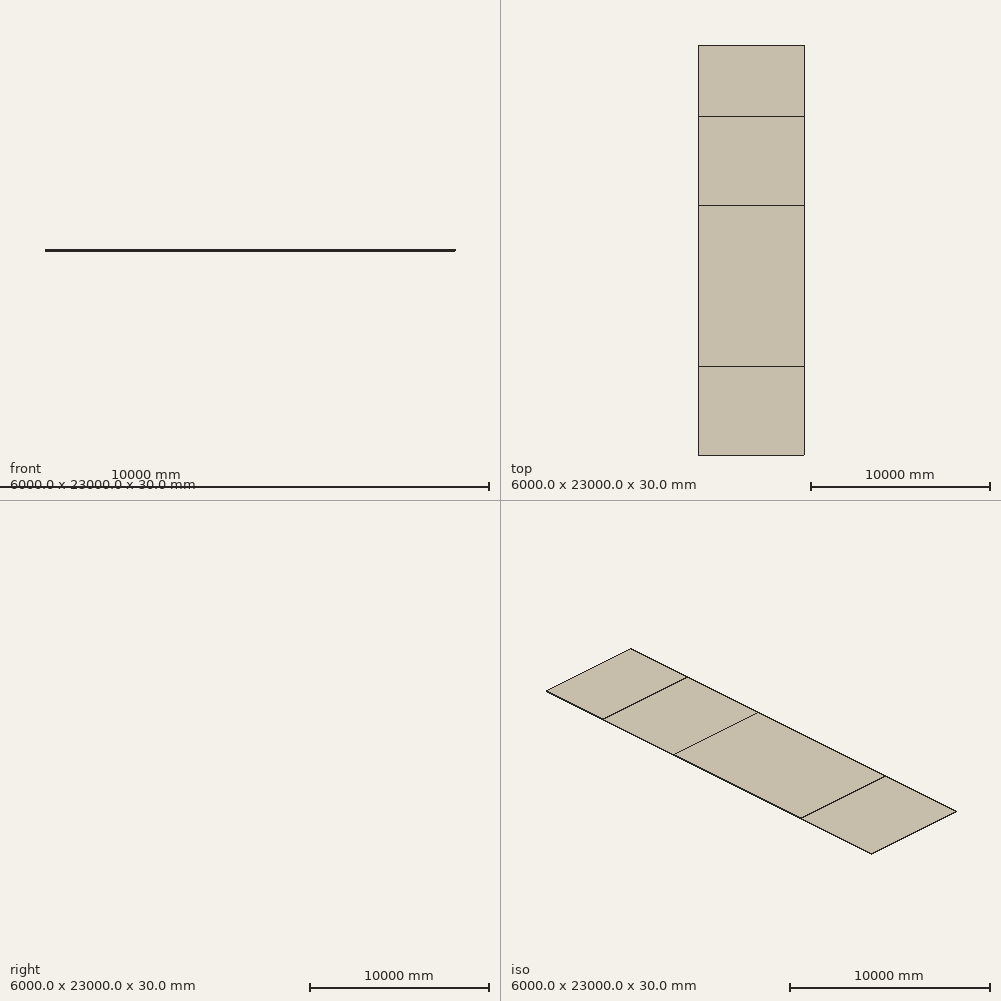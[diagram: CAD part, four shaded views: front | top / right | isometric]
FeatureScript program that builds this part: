
annotation { "Feature Type Name" : "Feature", "Feature Type Description" : "" }
export const myFeature = defineFeature(function(context is Context, id is Id, definition is map)
    precondition{}
    {
        {
            var Q0;
            Q0=qCreatedBy(makeId("Top.planeOp"),FACE);
            var sketch = newSketch(context, id + "F0", { "sketchPlane" : qUnion([Q0])});
            skLineSegment(sketch, "E0.bottom", {"start": v(0, 0) * mm, "end": v(-6000, 0) * mm});
            skLineSegment(sketch, "E0.top", {"start": v(0, 23000) * mm, "end": v(-6000, 23000) * mm});
            skLineSegment(sketch, "E0.left", {"start": v(0, 0) * mm, "end": v(0, 23000) * mm});
            skLineSegment(sketch, "E0.right", {"start": v(-6000, 0) * mm, "end": v(-6000, 23000) * mm});
            skSolve(sketch);
        }
        {
            var Q0;
            Q0=makeQuery(id+"F0.imprint","IMPRINT",FACE,{"disambiguationData":[TD([[makeQuery(id+"F0.imprint","IMPRINT",EDGE,{"derivedFrom":sQuery(id+"F0.wireOp",EDGE,"E0.bottom")}),-1.0]])]});
            extrude(context, id + "F1", {"entities" : qUnion([Q0]), "depth" : 30 * mm, "offsetDistance" : 25 * mm});
        }
        {
            var Q0;
            Q0=makeQuery(id+"F1.opExtrude","CAP_FACE",FACE,{"disambiguationData":[OSD([sQuery(id+"F0.wireOp",EDGE,"E0.bottom"),sQuery(id+"F0.wireOp",EDGE,"E0.top"),sQuery(id+"F0.wireOp",EDGE,"E0.left"),sQuery(id+"F0.wireOp",EDGE,"E0.right")])],"isStart":false});
            var sketch = newSketch(context, id + "F2", { "sketchPlane" : qUnion([Q0])});
            skLineSegment(sketch, "E1", {"start": v(-6000, 23000) * mm, "end": v(-6000, 19000) * mm});
            skLineSegment(sketch, "E2", {"start": v(-6000, 19000) * mm, "end": v(0, 19000) * mm});
            skLineSegment(sketch, "E3", {"start": v(0, 19000) * mm, "end": v(0, 23000) * mm});
            skLineSegment(sketch, "E4", {"start": v(0, 23000) * mm, "end": v(-6000, 23000) * mm});
            skLineSegment(sketch, "E5", {"start": v(-6000, 19000) * mm, "end": v(-6000, 14000) * mm});
            skLineSegment(sketch, "E6", {"start": v(-6000, 14000) * mm, "end": v(0, 14000) * mm});
            skLineSegment(sketch, "E7", {"start": v(0, 14000) * mm, "end": v(0, 19000) * mm});
            skLineSegment(sketch, "E8", {"start": v(-6000, 0) * mm, "end": v(-6000, 5000) * mm});
            skLineSegment(sketch, "E9", {"start": v(-6000, 5000) * mm, "end": v(0, 5000) * mm});
            skLineSegment(sketch, "E10", {"start": v(0, 5000) * mm, "end": v(0, 0) * mm});
            skLineSegment(sketch, "E11", {"start": v(0, 0) * mm, "end": v(-6000, 0) * mm});
            skLineSegment(sketch, "E12", {"start": v(-6000, 14000) * mm, "end": v(-6000, 5000) * mm});
            skSolve(sketch);
        }
        {
            var Q0;
            Q0=makeQuery(id+"F2.imprint","IMPRINT",FACE,{"disambiguationData":[TD([[makeQuery(id+"F2.imprint","IMPRINT",EDGE,{"derivedFrom":sQuery(id+"F2.wireOp",EDGE,"E2")}),-1.0]])]});
            var Q1;
            Q1=makeQuery(id+"F2.imprint","IMPRINT",FACE,{"disambiguationData":[TD([[makeQuery(id+"F2.imprint","IMPRINT",EDGE,{"derivedFrom":sQuery(id+"F2.wireOp",EDGE,"E8")}),-1.0]])]});
            extrude(context, id + "F3", {"entities" : qUnion([Q0, Q1]), "operationType" : NewBodyOperationType.REMOVE, "oppositeDirection" : true, "depth" : 10 * mm, "offsetDistance" : 25 * mm});
        }
    });
